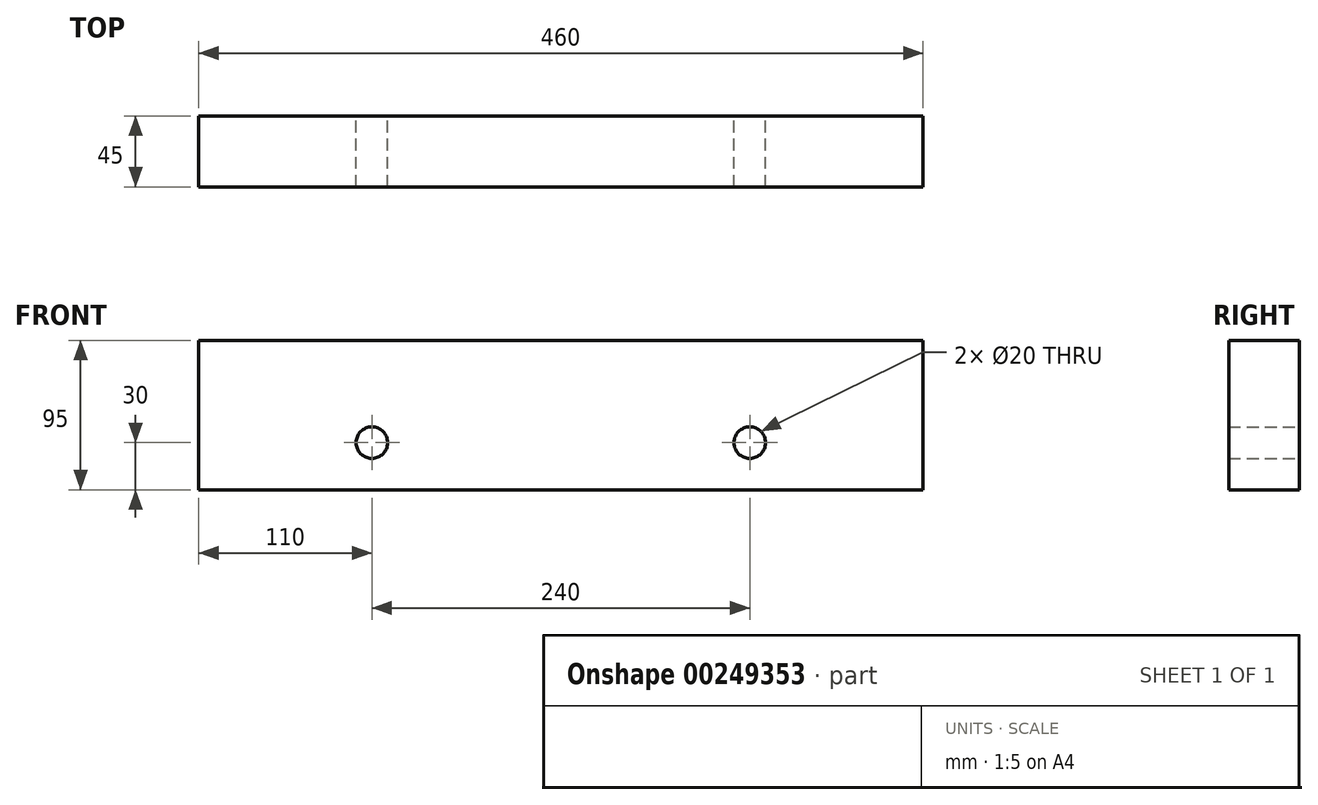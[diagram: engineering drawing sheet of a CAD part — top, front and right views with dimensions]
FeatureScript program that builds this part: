
annotation { "Feature Type Name" : "Feature", "Feature Type Description" : "" }
export const myFeature = defineFeature(function(context is Context, id is Id, definition is map)
    precondition{}
    {
        {
            var Q0;
            Q0=qCreatedBy(makeId("Front.planeOp"),FACE);
            var sketch = newSketch(context, id + "F0", { "sketchPlane" : qUnion([Q0])});
            skLineSegment(sketch, "E0.bottom", {"start": v(230, 47.5) * mm, "end": v(-230, 47.5) * mm});
            skLineSegment(sketch, "E0.top", {"start": v(230, -47.5) * mm, "end": v(-230, -47.5) * mm});
            skLineSegment(sketch, "E0.left", {"start": v(230, 47.5) * mm, "end": v(230, -47.5) * mm});
            skLineSegment(sketch, "E0.right", {"start": v(-230, 47.5) * mm, "end": v(-230, -47.5) * mm});
            skPoint(sketch, "E0.middle", {"position": v(0, 0) * mm});
            skCircle(sketch, "E1", {"center": v(-120, -17.5) * mm, "radius": 10 * mm});
            skCircle(sketch, "E2", {"center": v(120, -17.5) * mm, "radius": 10 * mm});
            skSolve(sketch);
        }
        {
            var Q0;
            Q0=makeQuery(id+"F0.imprint","IMPRINT",FACE,{"disambiguationData":[TD([[makeQuery(id+"F0.imprint","IMPRINT",EDGE,{"derivedFrom":sQuery(id+"F0.wireOp",EDGE,"E0.bottom")}),1.0]])]});
            extrude(context, id + "F1", {"entities" : qUnion([Q0]), "depth" : 45 * mm});
        }
    });
